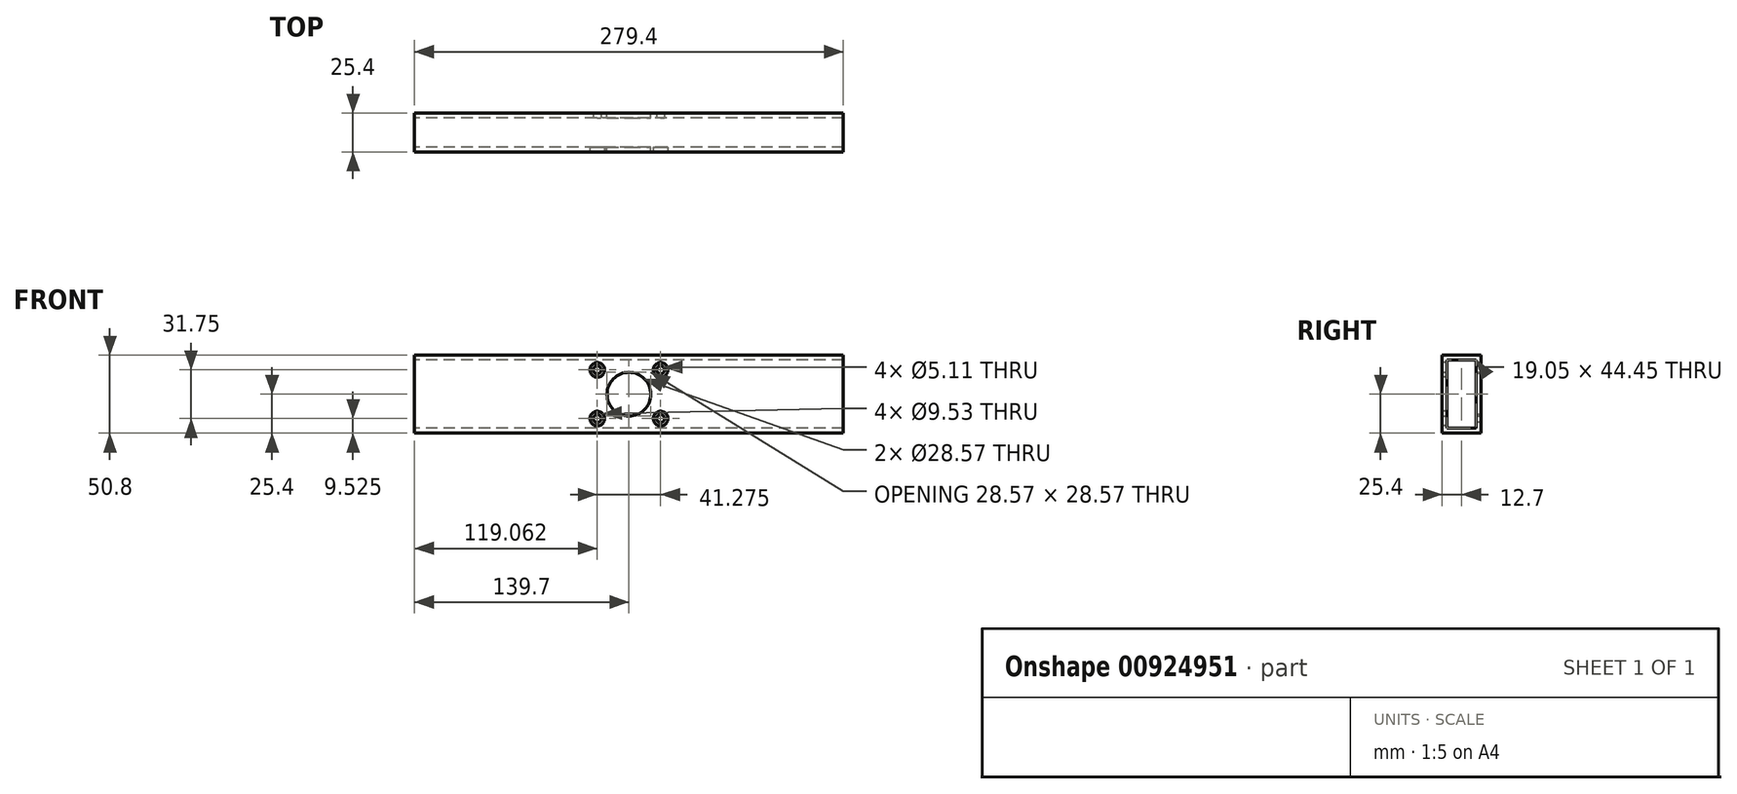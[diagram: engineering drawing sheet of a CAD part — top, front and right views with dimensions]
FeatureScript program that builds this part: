
annotation { "Feature Type Name" : "Feature", "Feature Type Description" : "" }
export const myFeature = defineFeature(function(context is Context, id is Id, definition is map)
    precondition{}
    {
        {
            var Q0;
            Q0=qCreatedBy(makeId("Right.planeOp"),FACE);
            var sketch = newSketch(context, id + "F0", { "sketchPlane" : qUnion([Q0])});
            skLineSegment(sketch, "E0.bottom", {"start": v(0, 25.4) * mm, "end": v(-25.4, 25.4) * mm});
            skLineSegment(sketch, "E0.top", {"start": v(0, -25.4) * mm, "end": v(-25.4, -25.4) * mm});
            skLineSegment(sketch, "E0.left", {"start": v(0, 25.4) * mm, "end": v(0, -25.4) * mm});
            skLineSegment(sketch, "E0.right", {"start": v(-25.4, 25.4) * mm, "end": v(-25.4, -25.4) * mm});
            skPoint(sketch, "E0.middle", {"position": v(-12.7, 0) * mm});
            skLineSegment(sketch, "E1.bottom", {"start": v(-22.23, 22.23) * mm, "end": v(-3.18, 22.23) * mm});
            skLineSegment(sketch, "E1.top", {"start": v(-22.22, -22.23) * mm, "end": v(-3.17, -22.23) * mm});
            skLineSegment(sketch, "E1.left", {"start": v(-22.23, 22.23) * mm, "end": v(-22.23, -22.23) * mm});
            skLineSegment(sketch, "E1.right", {"start": v(-3.18, 22.23) * mm, "end": v(-3.17, -22.23) * mm});
            skSolve(sketch);
        }
        {
            var Q0;
            Q0 = qSketchRegion(id + "F0", true);
            extrude(context, id + "F1", {"entities" : qUnion([Q0]), "depth" : 139.7 * mm, "offsetDistance" : 25.4 * mm, "hasSecondDirection" : true, "secondDirectionOppositeDirection" : true, "secondDirectionDepth" : 139.7 * mm});
        }
        {
            var Q0;
            Q0=qCreatedBy(makeId("Front.planeOp"),FACE);
            var sketch = newSketch(context, id + "F2", { "sketchPlane" : qUnion([Q0])});
            skCircle(sketch, "E2", {"center": v(0, 0) * mm, "radius": 14.29 * mm});
            skSolve(sketch);
        }
        {
            var Q0;
            Q0 = qSketchRegion(id + "F2", true);
            extrude(context, id + "F3", {"entities" : qUnion([Q0]), "operationType" : NewBodyOperationType.REMOVE, "depth" : 25.4 * mm, "offsetDistance" : 25.4 * mm});
        }
        {
            var Q0;
            Q0=makeQuery(id+"F1.opExtrude","SWEPT_FACE",FACE,{"disambiguationData":[OSD([sQuery(id+"F0.wireOp",EDGE,"E0.right")])]});
            var sketch = newSketch(context, id + "F4", { "sketchPlane" : qUnion([Q0])});
            skLineSegment(sketch, "E3.bottom", {"start": v(20.64, 15.87) * mm, "end": v(-20.64, 15.87) * mm, "construction": true});
            skLineSegment(sketch, "E3.top", {"start": v(20.64, -15.88) * mm, "end": v(-20.64, -15.88) * mm, "construction": true});
            skLineSegment(sketch, "E3.left", {"start": v(20.64, 15.87) * mm, "end": v(20.64, -15.88) * mm, "construction": true});
            skLineSegment(sketch, "E3.right", {"start": v(-20.64, 15.87) * mm, "end": v(-20.64, -15.88) * mm, "construction": true});
            skPoint(sketch, "E3.middle", {"position": v(0, 0) * mm});
            skCircle(sketch, "E4", {"center": v(20.64, -15.88) * mm, "radius": 2.55 * mm});
            skCircle(sketch, "E5", {"center": v(20.64, 15.87) * mm, "radius": 2.55 * mm});
            skCircle(sketch, "E6", {"center": v(-20.64, 15.87) * mm, "radius": 2.55 * mm});
            skCircle(sketch, "E7", {"center": v(-20.64, -15.88) * mm, "radius": 2.55 * mm});
            skSolve(sketch);
        }
        {
            var Q0;
            Q0 = qSketchRegion(id + "F4", true);
            var Q1;
            Q1=makeQuery(id+"F1.opExtrude","SWEPT_FACE",FACE,{"disambiguationData":[OSD([sQuery(id+"F0.wireOp",EDGE,"E1.left")])]});
            extrude(context, id + "F5", {"entities" : qUnion([Q0]), "operationType" : NewBodyOperationType.REMOVE, "oppositeDirection" : true, "depth" : 25.4 * mm, "endBoundEntityFace" : qUnion([Q1]), "offsetDistance" : 25.4 * mm});
        }
        {
            var Q0;
            Q0=makeQuery(id+"F1.opExtrude","SWEPT_FACE",FACE,{"disambiguationData":[OSD([sQuery(id+"F0.wireOp",EDGE,"E0.right")])]});
            var sketch = newSketch(context, id + "F6", { "sketchPlane" : qUnion([Q0])});
            skCircle(sketch, "E8", {"center": v(20.64, 15.87) * mm, "radius": 4.76 * mm});
            skCircle(sketch, "E9", {"center": v(20.64, -15.88) * mm, "radius": 4.76 * mm});
            skCircle(sketch, "E10", {"center": v(-20.64, -15.88) * mm, "radius": 4.76 * mm});
            skCircle(sketch, "E11", {"center": v(-20.64, 15.87) * mm, "radius": 4.76 * mm});
            skSolve(sketch);
        }
        {
            var Q0;
            Q0 = qSketchRegion(id + "F6", true);
            extrude(context, id + "F7", {"entities" : qUnion([Q0]), "operationType" : NewBodyOperationType.REMOVE, "oppositeDirection" : true, "depth" : 3.17 * mm, "offsetDistance" : 25.4 * mm});
        }
    });
